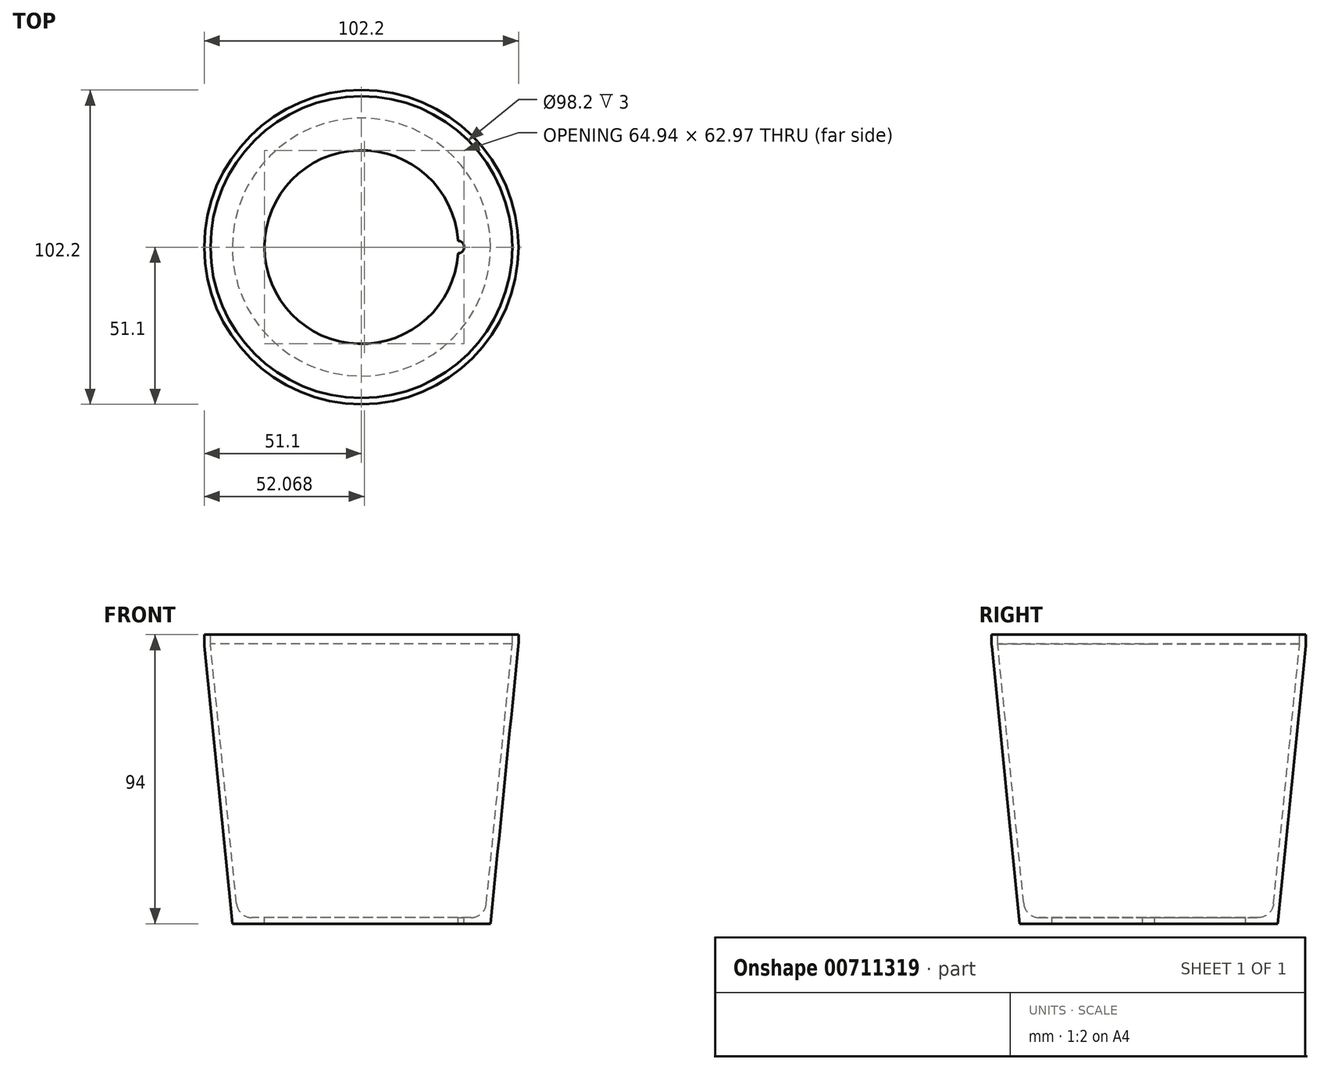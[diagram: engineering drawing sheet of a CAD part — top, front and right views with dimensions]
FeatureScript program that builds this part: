
annotation { "Feature Type Name" : "Feature", "Feature Type Description" : "" }
export const myFeature = defineFeature(function(context is Context, id is Id, definition is map)
    precondition{}
    {
        {
            var Q0;
            Q0=qCreatedBy(makeId("Front.planeOp"),FACE);
            var sketch = newSketch(context, id + "F0", { "sketchPlane" : qUnion([Q0])});
            skLineSegment(sketch, "E0", {"start": v(-31.5, 0) * mm, "end": v(-41.99, 0) * mm});
            skLineSegment(sketch, "E1", {"start": v(-35.65, 2) * mm, "end": v(-31.5, 2) * mm});
            skLineSegment(sketch, "E2", {"start": v(-31.5, 2) * mm, "end": v(-31.5, 0) * mm});
            skLineSegment(sketch, "E3", {"start": v(-51.05, 90.4) * mm, "end": v(-41.99, 0) * mm});
            skLineSegment(sketch, "E4", {"start": v(-49.1, 91) * mm, "end": v(-40.63, 6.5) * mm});
            skLineSegment(sketch, "E5", {"start": v(-51.1, 91.4) * mm, "end": v(-51.1, 94) * mm});
            skLineSegment(sketch, "E6", {"start": v(-51.1, 94) * mm, "end": v(-49.1, 94) * mm});
            skLineSegment(sketch, "E7", {"start": v(-49.1, 94) * mm, "end": v(-49.1, 91) * mm});
            skLineSegment(sketch, "E8", {"start": v(0, 0) * mm, "end": v(0, -22.8) * mm});
            skPoint(sketch, "E9.visualSharp", {"position": v(-40.18, 2) * mm});
            skArc(sketch, "E9.filletArc", {"start": v(-40.63, 6.5) * mm, "mid": v(-39, 3.3) * mm, "end": v(-35.65, 2) * mm});
            skPoint(sketch, "E10.visualSharp", {"position": v(-51.1, 90.9) * mm});
            skArc(sketch, "E10.filletArc", {"start": v(-51.1, 91.4) * mm, "mid": v(-51.09, 90.9) * mm, "end": v(-51.05, 90.4) * mm});
            skSolve(sketch);
        }
        {
            var Q0;
            Q0=makeQuery(id+"F0.imprint","IMPRINT",FACE,{"disambiguationData":[TD([[makeQuery(id+"F0.imprint","IMPRINT",EDGE,{"derivedFrom":sQuery(id+"F0.wireOp",EDGE,"E0")}),-1.0]])]});
            var Q1;
            Q1=sQuery(id+"F0.wireOp",EDGE,"E8");
            revolve(context, id + "F1", {"surfaceOperationType" : NewSurfaceOperationType.NEW, "entities" : qUnion([Q0]), "axis" : qUnion([Q1]), "revolveType" : RevolveType.FULL});
        }
        {
            var Q0;
            Q0=makeQuery(id+"F1.opRevolve","SWEPT_FACE",FACE,{"disambiguationData":[OSD([sQuery(id+"F0.wireOp",EDGE,"E1")])]});
            var sketch = newSketch(context, id + "F2", { "sketchPlane" : qUnion([Q0])});
            skPoint(sketch, "E11", {"position": v(31.44, 2) * mm});
            skPoint(sketch, "E12", {"position": v(31.44, -2) * mm});
            skArc(sketch, "E13", {"start": v(31.44, -2) * mm, "mid": v(33.44, 0) * mm, "end": v(31.44, 2) * mm});
            skSolve(sketch);
        }
        {
            var Q0;
            {var subQ0=sQuery(id+"F2.wireOp",EDGE,"E13");Q0=makeQuery(id+"F2.imprint","IMPRINT",FACE,{"disambiguationData":[TD([[makeQuery(id+"F2.imprint","IMPRINT",EDGE,{"derivedFrom":subQ0}),1.0]])]});}
            extrude(context, id + "F3", {"entities" : qUnion([Q0]), "operationType" : NewBodyOperationType.REMOVE, "endBound" : BoundingType.THROUGH_ALL, "oppositeDirection" : true, "depth" : 25 * mm, "offsetDistance" : 25 * mm});
        }
    });
